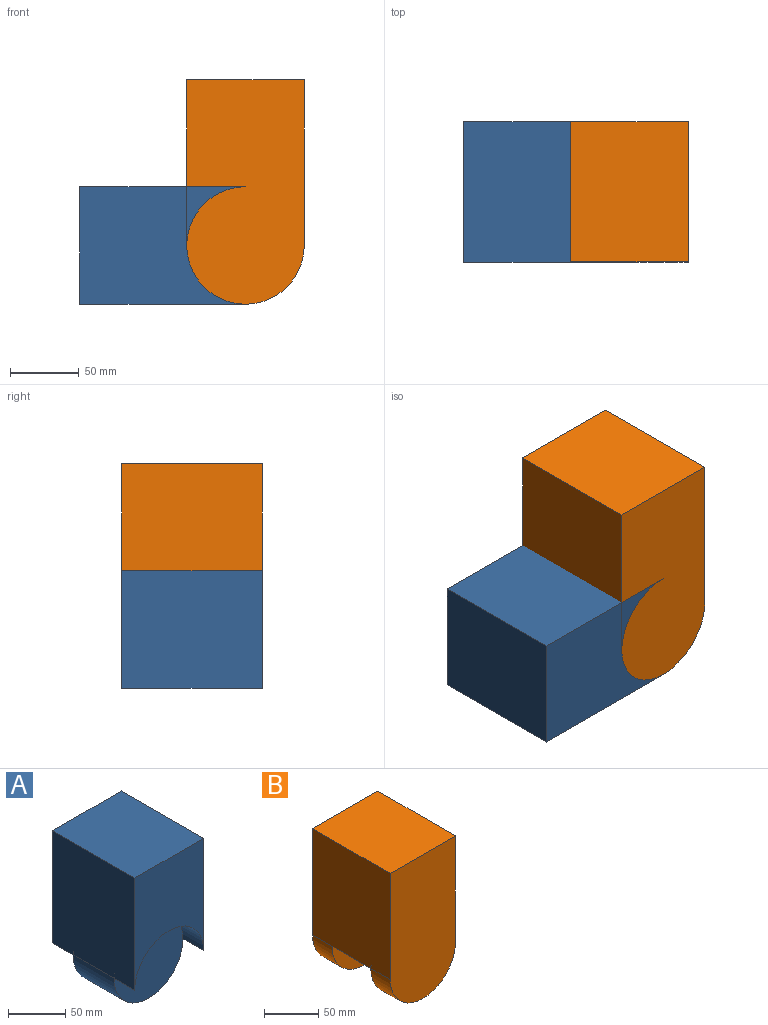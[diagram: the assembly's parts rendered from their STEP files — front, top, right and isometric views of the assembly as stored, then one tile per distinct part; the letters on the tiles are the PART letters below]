
ASSEMBLY  parts=2 mates=1
PART A: 10 faces, bbox 85.2x101.6x162.8 mm
  f0: plane 120.18x85.19mm, normal (0,1,0), area 7388.1mm2, adj f2,f3,f4,f8
  f1: cylinder r=42.6mm len=85.19mm, axis (0,1,0), area 6798.1mm2, adj f2,f3,f7,f9
  f2: plane 120.18x101.6mm, normal (-1,0,0), area 12210mm2, adj f0,f1,f4,f5,f6,f8
  f3: plane 120.18x101.6mm, normal (1,0,0), area 12210mm2, adj f0,f1,f4,f5,f6,f8
  f4: plane 101.6x85.19mm, normal (0,0,1), area 8655.6mm2, adj f0,f2,f3,f5
  f5: plane 120.18x85.19mm, normal (0,-1,0), area 7388.1mm2, adj f2,f3,f4,f6
  f6: cylinder r=42.6mm len=85.19mm, axis (0,-1,0), area 3399mm2, adj f2,f3,f5,f7
  f7: plane 85.19x85.19mm, normal (0,-1,0), area 5700.3mm2, adj f1,f6
  f8: cylinder r=42.6mm len=85.19mm, axis (0,1,0), area 3399mm2, adj f0,f2,f3,f9
  f9: plane 85.19x85.19mm, normal (0,1,0), area 5700.3mm2, adj f1,f8
PART B: 10 faces, bbox 85.2x101.6x162.8 mm
  f0: cylinder r=42.6mm len=85.19mm, axis (0,1,0), area 3399mm2, adj f1,f3,f6,f8
  f1: plane 120.18x101.6mm, normal (-1,0,0), area 12210mm2, adj f0,f2,f4,f5,f6,f7
  f2: cylinder r=42.6mm len=85.19mm, axis (0,1,0), area 3399mm2, adj f1,f3,f5,f9
  f3: plane 120.18x101.6mm, normal (1,0,0), area 12210mm2, adj f0,f2,f4,f5,f6,f7
  f4: plane 101.6x85.19mm, normal (0,0,1), area 8655.6mm2, adj f1,f3,f5,f6
  f5: plane 162.77x85.19mm, normal (0,-1,0), area 13088.4mm2, adj f1,f2,f3,f4
  f6: plane 162.77x85.19mm, normal (0,1,0), area 13088.4mm2, adj f0,f1,f3,f4
  f7: cylinder r=42.6mm len=85.19mm, axis (0,-1,0), area 6798.1mm2, adj f1,f3,f8,f9
  f8: plane 85.19x85.19mm, normal (0,-1,0), area 5700.3mm2, adj f0,f7
  f9: plane 85.19x85.19mm, normal (0,1,0), area 5700.3mm2, adj f2,f7
PLACE A rot(axis=(0,-1,0),90deg) t=(-185.51,-80,-71.48)mm
PLACE B t=(-125.42,-80,-11.39)mm fixed
MATE revolute B.f0 <-> A.f1  axis (0,1,0) through (-125.42,-105.4,-71.48)mm
